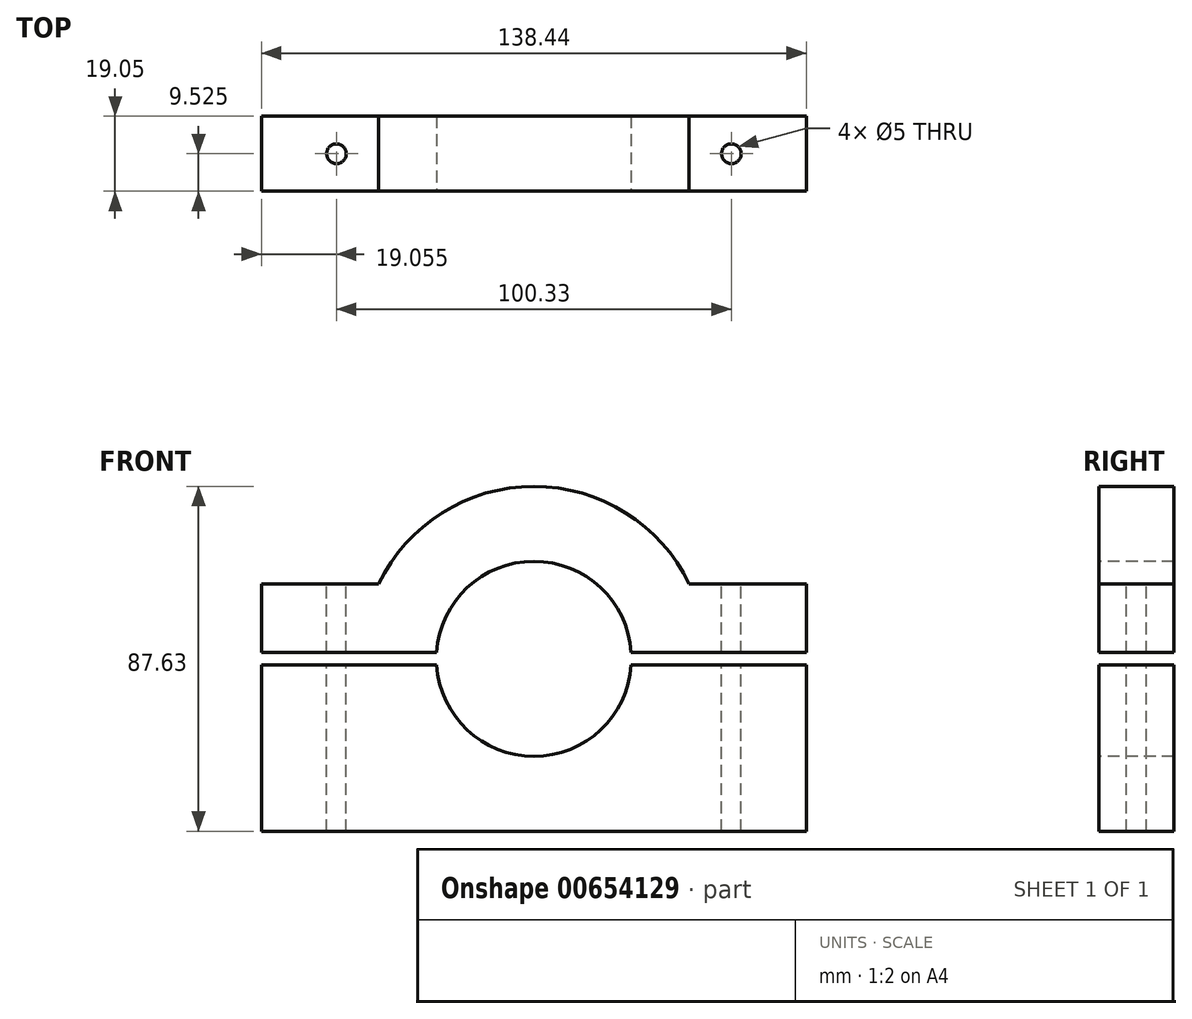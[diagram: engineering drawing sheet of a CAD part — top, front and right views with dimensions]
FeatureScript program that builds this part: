
annotation { "Feature Type Name" : "Feature", "Feature Type Description" : "" }
export const myFeature = defineFeature(function(context is Context, id is Id, definition is map)
    precondition{}
    {
        {
            var Q0;
            Q0=qCreatedBy(makeId("Front.planeOp"),FACE);
            var sketch = newSketch(context, id + "F0", { "sketchPlane" : qUnion([Q0])});
            skCircle(sketch, "E0", {"center": v(0, 0) * mm, "radius": 24.77 * mm});
            skArc(sketch, "E1", {"start": v(39.46, 19.05) * mm, "mid": v(0, 43.82) * mm, "end": v(-39.46, 19.05) * mm});
            skLineSegment(sketch, "E2.bottom", {"start": v(-69.22, 19.05) * mm, "end": v(-39.46, 19.05) * mm});
            skLineSegment(sketch, "E2.top", {"start": v(-69.22, -43.82) * mm, "end": v(69.22, -43.82) * mm});
            skLineSegment(sketch, "E2.left", {"start": v(-69.22, 19.05) * mm, "end": v(-69.22, -43.82) * mm});
            skLineSegment(sketch, "E2.right", {"start": v(69.22, 19.05) * mm, "end": v(69.22, -43.82) * mm});
            skLineSegment(sketch, "E3.trimOffspring", {"start": v(39.46, 19.05) * mm, "end": v(69.22, 19.05) * mm});
            skSolve(sketch);
        }
        {
            var Q0;
            Q0=makeQuery(id+"F0.imprint","IMPRINT",FACE,{"disambiguationData":[TD([[makeQuery(id+"F0.imprint","IMPRINT",EDGE,{"derivedFrom":sQuery(id+"F0.wireOp",EDGE,"E0")}),-1.0]])]});
            extrude(context, id + "F1", {"entities" : qUnion([Q0]), "oppositeDirection" : true, "depth" : 19.05 * mm, "offsetDistance" : 25.4 * mm});
        }
        {
            var Q0;
            Q0=makeQuery(id+"F1.opExtrude","CAP_FACE",FACE,{"disambiguationData":[OSD([sQuery(id+"F0.wireOp",EDGE,"E0"),sQuery(id+"F0.wireOp",EDGE,"E1"),sQuery(id+"F0.wireOp",EDGE,"E2.bottom"),sQuery(id+"F0.wireOp",EDGE,"E2.top"),sQuery(id+"F0.wireOp",EDGE,"E2.left"),sQuery(id+"F0.wireOp",EDGE,"E2.right"),sQuery(id+"F0.wireOp",EDGE,"E3.trimOffspring")])],"isStart":true});
            var sketch = newSketch(context, id + "F2", { "sketchPlane" : qUnion([Q0])});
            skLineSegment(sketch, "E4.bottom", {"start": v(-69.22, 1.59) * mm, "end": v(69.22, 1.59) * mm});
            skLineSegment(sketch, "E4.top", {"start": v(-69.22, -1.59) * mm, "end": v(69.22, -1.59) * mm});
            skLineSegment(sketch, "E4.left", {"start": v(-69.22, 1.59) * mm, "end": v(-69.22, -1.59) * mm});
            skLineSegment(sketch, "E4.right", {"start": v(69.22, 1.59) * mm, "end": v(69.22, -1.59) * mm});
            skSolve(sketch);
        }
        {
            var Q0;
            Q0 = qSketchRegion(id + "F2", true);
            extrude(context, id + "F3", {"entities" : qUnion([Q0]), "operationType" : NewBodyOperationType.REMOVE, "oppositeDirection" : true, "depth" : 25.4 * mm, "offsetDistance" : 25.4 * mm});
        }
        {
            var Q0;
            Q0=makeQuery(id+"F1.opExtrude","SWEPT_FACE",FACE,{"disambiguationData":[OSD([sQuery(id+"F0.wireOp",EDGE,"E2.bottom")])]});
            var sketch = newSketch(context, id + "F4", { "sketchPlane" : qUnion([Q0])});
            skCircle(sketch, "E5", {"center": v(-50.17, 9.53) * mm, "radius": 2.5 * mm});
            skPoint(sketch, "E5.centerSnap0", {"position": v(-69.22, 9.53) * mm});
            skCircle(sketch, "E6", {"center": v(50.17, 9.53) * mm, "radius": 2.5 * mm});
            skPoint(sketch, "E6.centerSnap0", {"position": v(-39.46, 9.53) * mm});
            skSolve(sketch);
        }
        {
            var Q0;
            Q0 = qSketchRegion(id + "F4", true);
            extrude(context, id + "F5", {"entities" : qUnion([Q0]), "operationType" : NewBodyOperationType.REMOVE, "oppositeDirection" : true, "depth" : 127 * mm, "offsetDistance" : 25.4 * mm});
        }
    });
